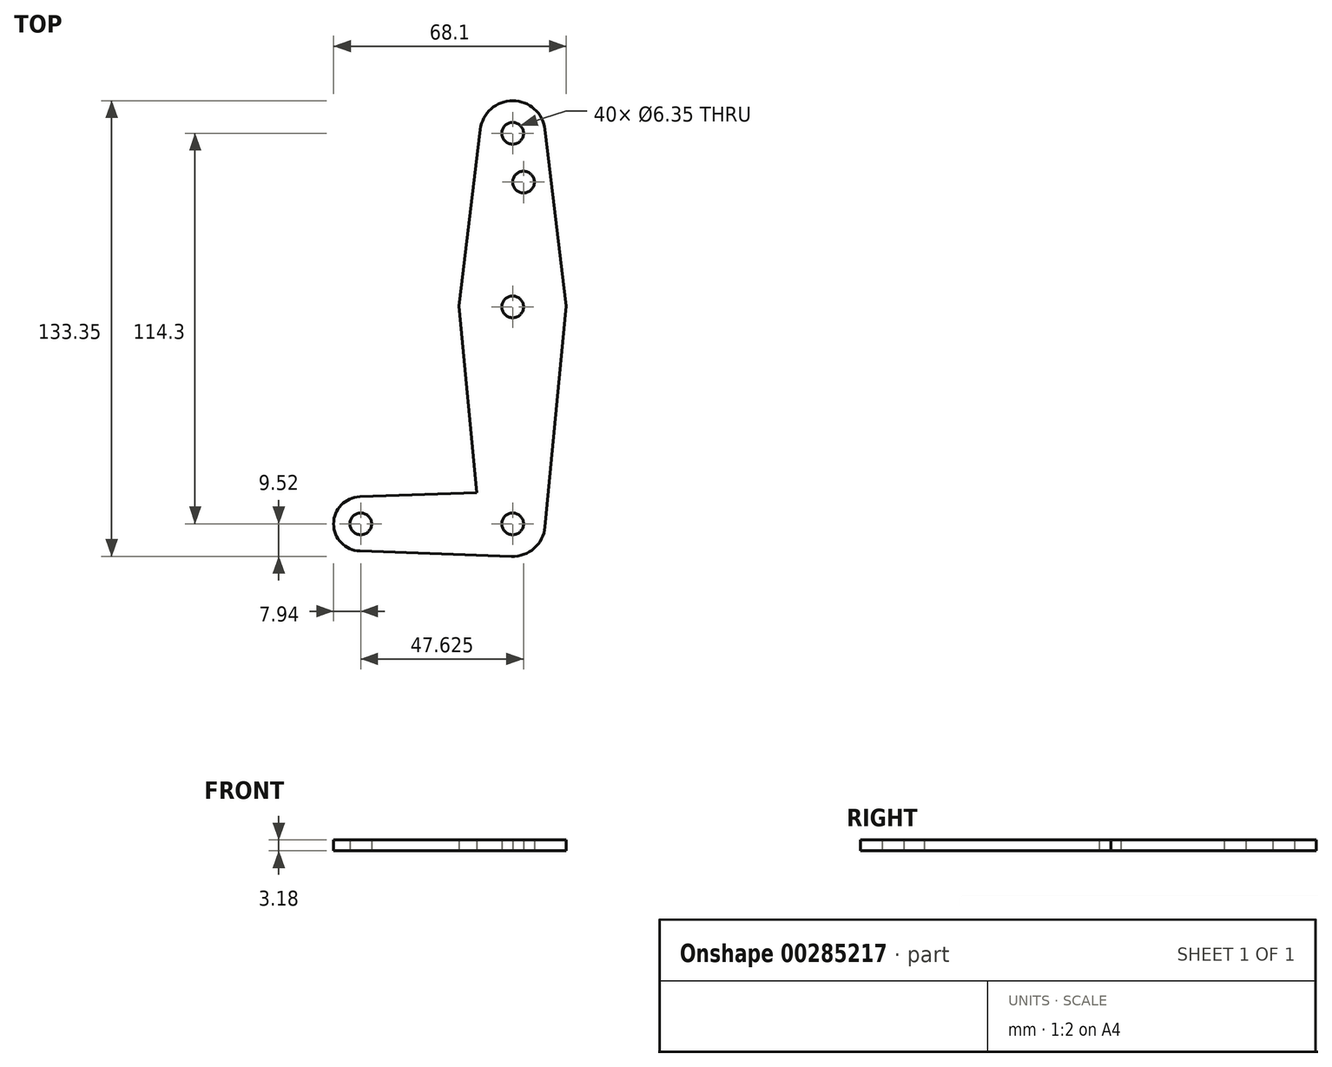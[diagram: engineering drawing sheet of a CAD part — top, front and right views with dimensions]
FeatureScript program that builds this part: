
annotation { "Feature Type Name" : "Feature", "Feature Type Description" : "" }
export const myFeature = defineFeature(function(context is Context, id is Id, definition is map)
    precondition{}
    {
        {
            var Q0;
            Q0=qCreatedBy(makeId("Top.planeOp"),FACE);
            var sketch = newSketch(context, id + "F0", { "sketchPlane" : qUnion([Q0])});
            skCircle(sketch, "E0", {"center": v(0, 0) * mm, "radius": 3.18 * mm});
            skCircle(sketch, "E1", {"center": v(-44.45, 0) * mm, "radius": 3.18 * mm});
            skCircle(sketch, "E2", {"center": v(0, 114.3) * mm, "radius": 3.18 * mm});
            skLineSegment(sketch, "E3", {"start": v(0, 114.3) * mm, "end": v(0, 0) * mm, "construction": true});
            skCircle(sketch, "E4", {"center": v(0, 63.5) * mm, "radius": 3.18 * mm});
            skCircle(sketch, "E5", {"center": v(-44.45, 0) * mm, "radius": 7.94 * mm});
            skCircle(sketch, "E6", {"center": v(0, 0) * mm, "radius": 9.53 * mm});
            skCircle(sketch, "E7", {"center": v(0, 63.5) * mm, "radius": 15.62 * mm});
            skCircle(sketch, "E8", {"center": v(0, 114.3) * mm, "radius": 9.53 * mm});
            skLineSegment(sketch, "E9", {"start": v(-44.73, -7.93) * mm, "end": v(-0.34, -9.52) * mm});
            skLineSegment(sketch, "E10", {"start": v(-44.73, 7.93) * mm, "end": v(-10.45, 9.16) * mm});
            skLineSegment(sketch, "E11", {"start": v(-15.71, 63.69) * mm, "end": v(-10.45, 9.16) * mm});
            skLineSegment(sketch, "E12", {"start": v(15.71, 63.69) * mm, "end": v(9.48, -0.91) * mm});
            skLineSegment(sketch, "E13", {"start": v(-9.46, 115.44) * mm, "end": v(-15.71, 63.69) * mm});
            skLineSegment(sketch, "E14", {"start": v(9.46, 115.44) * mm, "end": v(15.71, 63.69) * mm});
            skLineSegment(sketch, "E15.trimOffspring", {"start": v(-0.34, 9.52) * mm, "end": v(0, 9.53) * mm});
            skCircle(sketch, "E16", {"center": v(3.18, 100.01) * mm, "radius": 3.18 * mm});
            skSolve(sketch);
        }
        {
            var Q0;
            Q0 = qSketchRegion(id + "F0", true);
            extrude(context, id + "F1", {"entities" : qUnion([Q0]), "depth" : 3.17 * mm});
        }
    });
